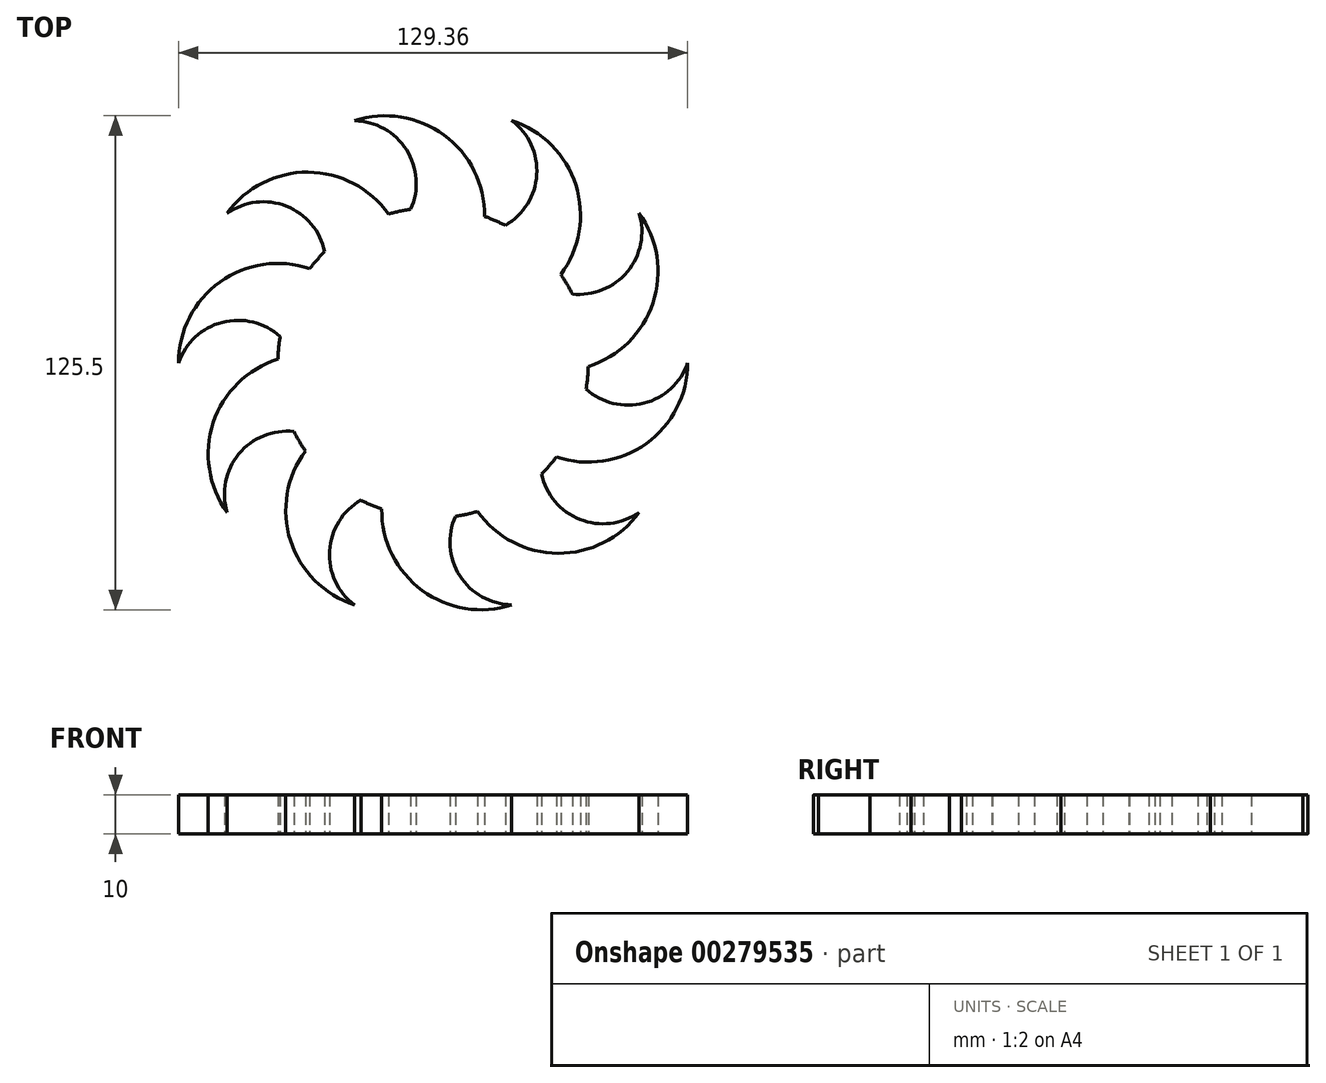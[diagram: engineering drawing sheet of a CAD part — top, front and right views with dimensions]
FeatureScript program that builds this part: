
annotation { "Feature Type Name" : "Feature", "Feature Type Description" : "" }
export const myFeature = defineFeature(function(context is Context, id is Id, definition is map)
    precondition{}
    {
        {
            var Q0;
            Q0=qCreatedBy(makeId("Top.planeOp"),FACE);
            var sketch = newSketch(context, id + "F0", { "sketchPlane" : qUnion([Q0])});
            skArc(sketch, "E0", {"start": v(-38.86, 6.65) * mm, "mid": v(-39.29, 3.34) * mm, "end": v(-39.43, 0) * mm});
            skArc(sketch, "E1", {"start": v(-31.34, 23.92) * mm, "mid": v(-54.15, 20.51) * mm, "end": v(-64.68, 0) * mm});
            skArc(sketch, "E2", {"start": v(-38.86, 6.65) * mm, "mid": v(-53.56, 10.28) * mm, "end": v(-64.68, 0) * mm});
            skArc(sketch, "E3.1.0", {"start": v(-39.42, 0.93) * mm, "mid": v(-55.86, -15.23) * mm, "end": v(-52.32, -38.02) * mm});
            skArc(sketch, "E3.1.1", {"start": v(-35.35, -17.46) * mm, "mid": v(-49.37, -23.17) * mm, "end": v(-52.32, -38.02) * mm});
            skArc(sketch, "E3.2.0", {"start": v(-32.43, -22.42) * mm, "mid": v(-36.24, -45.16) * mm, "end": v(-19.99, -61.51) * mm});
            skArc(sketch, "E3.2.1", {"start": v(-18.33, -34.9) * mm, "mid": v(-26.32, -47.76) * mm, "end": v(-19.99, -61.51) * mm});
            skArc(sketch, "E3.3.0", {"start": v(-13.06, -37.2) * mm, "mid": v(-2.78, -57.84) * mm, "end": v(19.99, -61.51) * mm});
            skArc(sketch, "E3.3.1", {"start": v(5.68, -39.02) * mm, "mid": v(6.78, -54.11) * mm, "end": v(19.99, -61.51) * mm});
            skArc(sketch, "E3.4.0", {"start": v(11.3, -37.77) * mm, "mid": v(31.75, -48.42) * mm, "end": v(52.32, -38.02) * mm});
            skArc(sketch, "E3.4.1", {"start": v(27.53, -28.22) * mm, "mid": v(37.3, -39.8) * mm, "end": v(52.32, -38.02) * mm});
            skArc(sketch, "E3.5.0", {"start": v(31.34, -23.92) * mm, "mid": v(54.15, -20.51) * mm, "end": v(64.68, 0) * mm});
            skArc(sketch, "E3.5.1", {"start": v(38.86, -6.65) * mm, "mid": v(53.56, -10.28) * mm, "end": v(64.68, 0) * mm});
            skArc(sketch, "E3.6.0", {"start": v(39.42, -0.93) * mm, "mid": v(55.86, 15.23) * mm, "end": v(52.32, 38.02) * mm});
            skArc(sketch, "E3.6.1", {"start": v(35.35, 17.46) * mm, "mid": v(49.37, 23.17) * mm, "end": v(52.32, 38.02) * mm});
            skArc(sketch, "E3.7.0", {"start": v(32.43, 22.42) * mm, "mid": v(36.24, 45.16) * mm, "end": v(19.99, 61.51) * mm});
            skArc(sketch, "E3.7.1", {"start": v(18.33, 34.9) * mm, "mid": v(26.32, 47.76) * mm, "end": v(19.99, 61.51) * mm});
            skArc(sketch, "E3.8.0", {"start": v(13.06, 37.2) * mm, "mid": v(2.78, 57.84) * mm, "end": v(-19.99, 61.51) * mm});
            skArc(sketch, "E3.8.1", {"start": v(-5.68, 39.02) * mm, "mid": v(-6.78, 54.11) * mm, "end": v(-19.99, 61.51) * mm});
            skArc(sketch, "E3.9.0", {"start": v(-11.3, 37.77) * mm, "mid": v(-31.75, 48.42) * mm, "end": v(-52.32, 38.02) * mm});
            skArc(sketch, "E3.9.1", {"start": v(-27.53, 28.22) * mm, "mid": v(-37.3, 39.8) * mm, "end": v(-52.32, 38.02) * mm});
            skArc(sketch, "E4.trimOffspring", {"start": v(-27.53, 28.22) * mm, "mid": v(-29.52, 26.14) * mm, "end": v(-31.34, 23.92) * mm});
            skArc(sketch, "E5.trimOffspring", {"start": v(-5.68, 39.02) * mm, "mid": v(-8.97, 38.4) * mm, "end": v(-12.18, 37.5) * mm});
            skArc(sketch, "E6.trimOffspring", {"start": v(18.33, 34.9) * mm, "mid": v(15.31, 36.33) * mm, "end": v(12.18, 37.5) * mm});
            skArc(sketch, "E7.trimOffspring", {"start": v(35.35, 17.46) * mm, "mid": v(33.74, 20.4) * mm, "end": v(31.9, 23.18) * mm});
            skArc(sketch, "E8.trimOffspring", {"start": v(38.86, -6.65) * mm, "mid": v(39.29, -3.34) * mm, "end": v(39.43, 0) * mm});
            skArc(sketch, "E9.trimOffspring", {"start": v(27.53, -28.22) * mm, "mid": v(29.82, -25.8) * mm, "end": v(31.9, -23.18) * mm});
            skArc(sketch, "E10.trimOffspring", {"start": v(5.68, -39.02) * mm, "mid": v(8.97, -38.4) * mm, "end": v(12.18, -37.5) * mm});
            skArc(sketch, "E11.trimOffspring", {"start": v(-18.33, -34.9) * mm, "mid": v(-15.31, -36.33) * mm, "end": v(-12.18, -37.5) * mm});
            skArc(sketch, "E12.trimOffspring", {"start": v(-35.35, -17.46) * mm, "mid": v(-33.74, -20.4) * mm, "end": v(-31.9, -23.18) * mm});
            skSolve(sketch);
        }
        {
            var Q0;
            Q0 = qSketchRegion(id + "F0", true);
            extrude(context, id + "F1", {"entities" : qUnion([Q0]), "depth" : 10 * mm});
        }
    });
